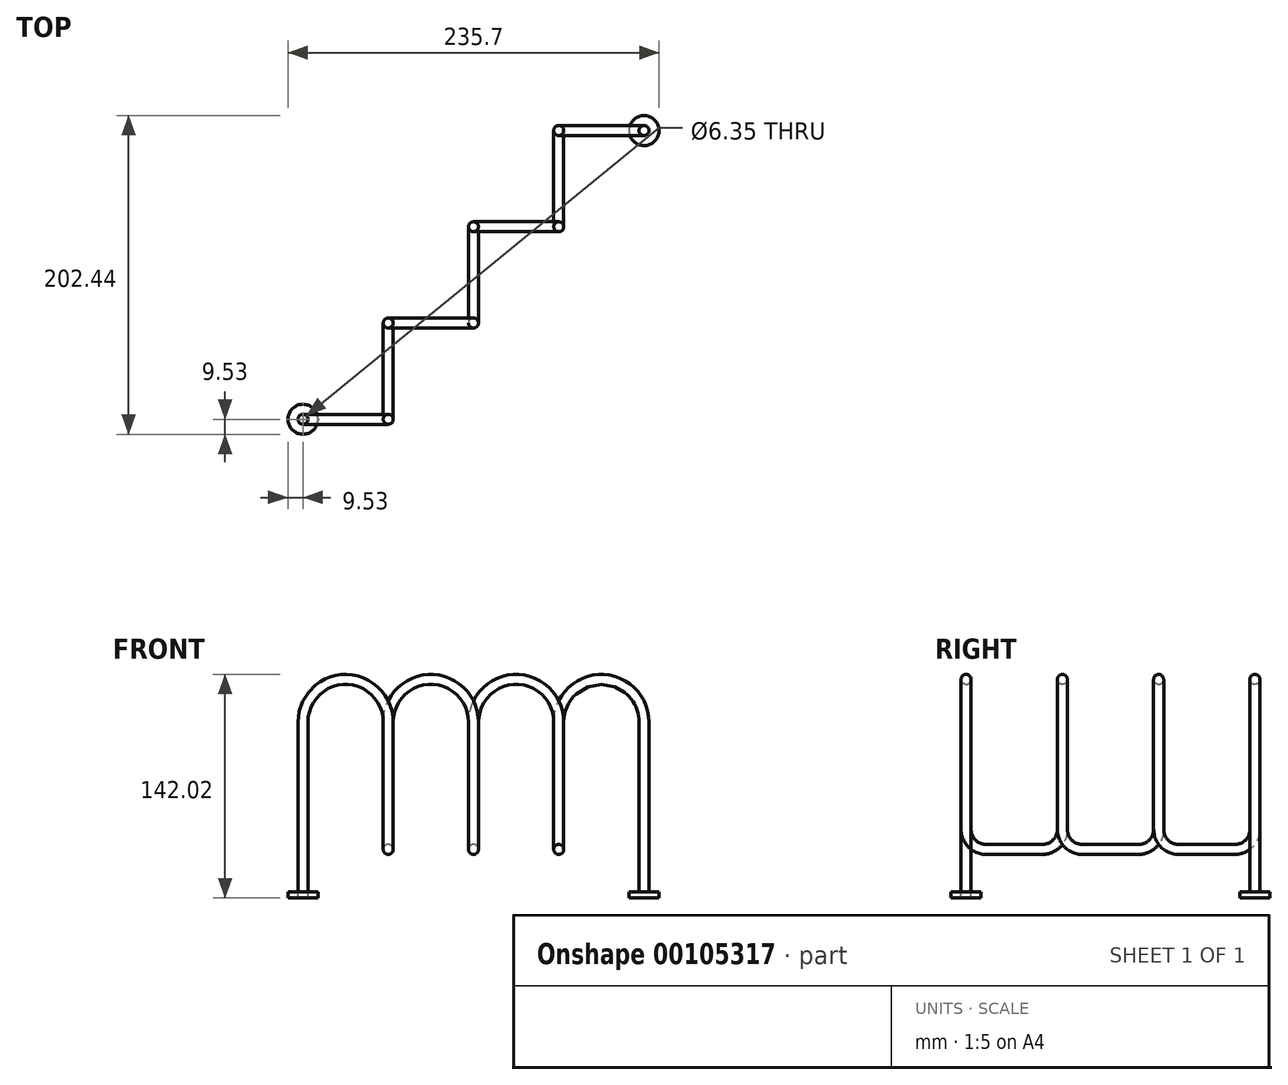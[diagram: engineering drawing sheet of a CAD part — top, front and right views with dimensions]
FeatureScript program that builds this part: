
annotation { "Feature Type Name" : "Feature", "Feature Type Description" : "" }
export const myFeature = defineFeature(function(context is Context, id is Id, definition is map)
    precondition{}
    {
        {
            var Q0;
            Q0=qCreatedBy(makeId("Front.planeOp"),FACE);
            var sketch = newSketch(context, id + "F0", { "sketchPlane" : qUnion([Q0])});
            skLineSegment(sketch, "E0", {"start": v(0, 0) * mm, "end": v(0, -19.05) * mm});
            skLineSegment(sketch, "E1", {"start": v(0, 0) * mm, "end": v(0, 88.9) * mm});
            skArc(sketch, "E2", {"start": v(54.17, 88.9) * mm, "mid": v(27.08, 115.98) * mm, "end": v(0, 88.9) * mm});
            skSolve(sketch);
        }
        {
            var Q0;
            Q0=sQuery(id+"F0.wireOp",VERTEX,"E2.start");
            var Q1;
            Q1=qCreatedBy(makeId("Right.planeOp"),FACE);
            cPlane(context, id + "F1", {"entities" : qUnion([Q0, Q1]), "cplaneType" : CPlaneType.PLANE_POINT, "offset" : 25.4 * mm, "width" : 152.4 * mm, "height" : 152.4 * mm});
        }
        {
            var Q0;
            Q0=qCreatedBy(id+"F1.planeOp",FACE);
            var sketch = newSketch(context, id + "F2", { "sketchPlane" : qUnion([Q0])});
            skLineSegment(sketch, "E3", {"start": v(0, 88.9) * mm, "end": v(0, 20.68) * mm});
            skArc(sketch, "E4", {"start": v(0, 20.68) * mm, "mid": v(3.72, 11.7) * mm, "end": v(12.7, 7.98) * mm});
            skLineSegment(sketch, "E5", {"start": v(12.7, 7.98) * mm, "end": v(48.44, 7.98) * mm});
            skArc(sketch, "E6", {"start": v(48.44, 7.98) * mm, "mid": v(57.42, 11.7) * mm, "end": v(61.14, 20.68) * mm});
            skSolve(sketch);
        }
        {
            var Q0;
            Q0=sQuery(id+"F2.wireOp",VERTEX,"E6.end");
            var Q1;
            Q1=qCreatedBy(makeId("Front.planeOp"),FACE);
            cPlane(context, id + "F3", {"entities" : qUnion([Q0, Q1]), "cplaneType" : CPlaneType.PLANE_POINT, "offset" : 25.4 * mm, "width" : 152.4 * mm, "height" : 152.4 * mm});
        }
        {
            var Q0;
            Q0=qCreatedBy(id+"F3.planeOp",FACE);
            var sketch = newSketch(context, id + "F4", { "sketchPlane" : qUnion([Q0])});
            skLineSegment(sketch, "E7", {"start": v(54.17, 20.68) * mm, "end": v(54.17, 88.9) * mm});
            skArc(sketch, "E8", {"start": v(108.32, 88.9) * mm, "mid": v(81.24, 115.98) * mm, "end": v(54.17, 88.9) * mm});
            skSolve(sketch);
        }
        {
            var Q0;
            Q0=sQuery(id+"F4.wireOp",VERTEX,"E8.start");
            var Q1;
            Q1=qCreatedBy(id+"F1.planeOp",FACE);
            cPlane(context, id + "F5", {"entities" : qUnion([Q0, Q1]), "cplaneType" : CPlaneType.PLANE_POINT, "offset" : 25.4 * mm, "width" : 152.4 * mm, "height" : 152.4 * mm});
        }
        {
            var Q0;
            Q0=qCreatedBy(id+"F5.planeOp",FACE);
            var sketch = newSketch(context, id + "F6", { "sketchPlane" : qUnion([Q0])});
            skLineSegment(sketch, "E9", {"start": v(61.14, 88.9) * mm, "end": v(61.14, 20.68) * mm});
            skArc(sketch, "E10", {"start": v(61.14, 20.68) * mm, "mid": v(64.86, 11.7) * mm, "end": v(73.84, 7.98) * mm});
            skLineSegment(sketch, "E11", {"start": v(73.84, 7.98) * mm, "end": v(109.58, 7.98) * mm});
            skArc(sketch, "E12", {"start": v(109.58, 7.98) * mm, "mid": v(118.56, 11.7) * mm, "end": v(122.28, 20.68) * mm});
            skSolve(sketch);
        }
        {
            var Q0;
            Q0=sQuery(id+"F6.wireOp",VERTEX,"E12.end");
            var Q1;
            Q1=qCreatedBy(makeId("Front.planeOp"),FACE);
            cPlane(context, id + "F7", {"entities" : qUnion([Q0, Q1]), "cplaneType" : CPlaneType.PLANE_POINT, "offset" : 25.4 * mm, "width" : 152.4 * mm, "height" : 152.4 * mm});
        }
        {
            var Q0;
            Q0=qCreatedBy(id+"F7.planeOp",FACE);
            var sketch = newSketch(context, id + "F8", { "sketchPlane" : qUnion([Q0])});
            skLineSegment(sketch, "E13", {"start": v(108.32, 20.68) * mm, "end": v(108.32, 88.9) * mm});
            skArc(sketch, "E14", {"start": v(162.47, 88.9) * mm, "mid": v(135.4, 115.98) * mm, "end": v(108.32, 88.9) * mm});
            skSolve(sketch);
        }
        {
            var Q0;
            Q0=sQuery(id+"F8.wireOp",VERTEX,"E14.start");
            var Q1;
            Q1=qCreatedBy(id+"F1.planeOp",FACE);
            cPlane(context, id + "F9", {"entities" : qUnion([Q0, Q1]), "cplaneType" : CPlaneType.PLANE_POINT, "offset" : 25.4 * mm, "width" : 152.4 * mm, "height" : 152.4 * mm});
        }
        {
            var Q0;
            Q0=qCreatedBy(id+"F9.planeOp",FACE);
            var sketch = newSketch(context, id + "F10", { "sketchPlane" : qUnion([Q0])});
            skLineSegment(sketch, "E15", {"start": v(122.28, 88.9) * mm, "end": v(122.28, 20.68) * mm});
            skArc(sketch, "E16", {"start": v(122.28, 20.68) * mm, "mid": v(126, 11.7) * mm, "end": v(134.98, 7.98) * mm});
            skLineSegment(sketch, "E17", {"start": v(134.98, 7.98) * mm, "end": v(170.72, 7.98) * mm});
            skArc(sketch, "E18", {"start": v(170.72, 7.98) * mm, "mid": v(179.7, 11.7) * mm, "end": v(183.42, 20.68) * mm});
            skSolve(sketch);
        }
        {
            var Q0;
            Q0=sQuery(id+"F10.wireOp",VERTEX,"E18.end");
            var Q1;
            Q1=qCreatedBy(makeId("Front.planeOp"),FACE);
            cPlane(context, id + "F11", {"entities" : qUnion([Q0, Q1]), "cplaneType" : CPlaneType.PLANE_POINT, "offset" : 25.4 * mm, "width" : 152.4 * mm, "height" : 152.4 * mm});
        }
        {
            var Q0;
            Q0=qCreatedBy(id+"F11.planeOp",FACE);
            var sketch = newSketch(context, id + "F12", { "sketchPlane" : qUnion([Q0])});
            skLineSegment(sketch, "E19", {"start": v(162.47, 20.68) * mm, "end": v(162.47, 88.9) * mm});
            skArc(sketch, "E20", {"start": v(216.63, 88.9) * mm, "mid": v(189.55, 115.98) * mm, "end": v(162.47, 88.9) * mm});
            skLineSegment(sketch, "E21", {"start": v(216.63, 88.9) * mm, "end": v(216.63, 0) * mm});
            skLineSegment(sketch, "E22", {"start": v(216.63, 0) * mm, "end": v(216.63, -19.05) * mm});
            skSolve(sketch);
        }
        {
            var Q0;
            Q0=sQuery(id+"F0.wireOp",VERTEX,"E0.end");
            var Q1;
            Q1=qCreatedBy(makeId("Top.planeOp"),FACE);
            cPlane(context, id + "F13", {"entities" : qUnion([Q0, Q1]), "cplaneType" : CPlaneType.PLANE_POINT, "offset" : 25.4 * mm, "width" : 152.4 * mm, "height" : 152.4 * mm});
        }
        {
            var Q0;
            Q0=qCreatedBy(id+"F13.planeOp",FACE);
            var sketch = newSketch(context, id + "F14", { "sketchPlane" : qUnion([Q0])});
            skCircle(sketch, "E23", {"center": v(0, 0) * mm, "radius": 3.18 * mm});
            skCircle(sketch, "E24", {"center": v(0, 0) * mm, "radius": 9.53 * mm});
            skSolve(sketch);
        }
        {
            var Q0;
            Q0=makeQuery(id+"F14.imprint","IMPRINT",FACE,{"disambiguationData":[TD([[makeQuery(id+"F14.imprint","IMPRINT",EDGE,{"derivedFrom":sQuery(id+"F14.wireOp",EDGE,"E23")}),1.0]])]});
            var Q1;
            Q1=sQuery(id+"F0.wireOp",EDGE,"E0");
            var Q2;
            Q2=sQuery(id+"F0.wireOp",EDGE,"E1");
            var Q3;
            Q3=sQuery(id+"F0.wireOp",EDGE,"E2");
            var Q4;
            Q4=sQuery(id+"F2.wireOp",EDGE,"E3");
            var Q5;
            Q5=sQuery(id+"F2.wireOp",EDGE,"E4");
            var Q6;
            Q6=sQuery(id+"F2.wireOp",EDGE,"E5");
            var Q7;
            Q7=sQuery(id+"F2.wireOp",EDGE,"E6");
            var Q8;
            Q8=sQuery(id+"F4.wireOp",EDGE,"E7");
            var Q9;
            Q9=sQuery(id+"F4.wireOp",EDGE,"E8");
            var Q10;
            Q10=sQuery(id+"F6.wireOp",EDGE,"E9");
            var Q11;
            Q11=sQuery(id+"F6.wireOp",EDGE,"E10");
            var Q12;
            Q12=sQuery(id+"F6.wireOp",EDGE,"E11");
            var Q13;
            Q13=sQuery(id+"F6.wireOp",EDGE,"E12");
            var Q14;
            Q14=sQuery(id+"F8.wireOp",EDGE,"E13");
            var Q15;
            Q15=sQuery(id+"F8.wireOp",EDGE,"E14");
            var Q16;
            Q16=sQuery(id+"F10.wireOp",EDGE,"E15");
            var Q17;
            Q17=sQuery(id+"F10.wireOp",EDGE,"E16");
            var Q18;
            Q18=sQuery(id+"F10.wireOp",EDGE,"E17");
            var Q19;
            Q19=sQuery(id+"F10.wireOp",EDGE,"E18");
            var Q20;
            Q20=sQuery(id+"F12.wireOp",EDGE,"E19");
            var Q21;
            Q21=sQuery(id+"F12.wireOp",EDGE,"E20");
            var Q22;
            Q22=sQuery(id+"F12.wireOp",EDGE,"E21");
            var Q23;
            Q23=sQuery(id+"F12.wireOp",EDGE,"E22");
            sweep(context, id + "F15", {"profiles" : qUnion([Q0]), "path" : qUnion([Q1, Q2, Q3, Q4, Q5, Q6, Q7, Q8, Q9, Q10, Q11, Q12, Q13, Q14, Q15, Q16, Q17, Q18, Q19, Q20, Q21, Q22, Q23])});
        }
        {
            var Q0;
            Q0 = qSketchRegion(id + "F14", true);
            extrude(context, id + "F16", {"entities" : qUnion([Q0]), "oppositeDirection" : true, "depth" : 3.8 * mm});
        }
        {
            var Q0;
            Q0=sQuery(id+"F12.wireOp",VERTEX,"E22.end");
            var Q1;
            Q1=qCreatedBy(id+"F13.planeOp",FACE);
            cPlane(context, id + "F17", {"entities" : qUnion([Q0, Q1]), "cplaneType" : CPlaneType.PLANE_POINT, "offset" : 25.4 * mm, "width" : 152.4 * mm, "height" : 152.4 * mm});
        }
        {
            var Q0;
            Q0=qCreatedBy(id+"F17.planeOp",FACE);
            var sketch = newSketch(context, id + "F18", { "sketchPlane" : qUnion([Q0])});
            skCircle(sketch, "E25", {"center": v(216.65, 183.38) * mm, "radius": 9.53 * mm});
            skSolve(sketch);
        }
        {
            var Q0;
            Q0 = qSketchRegion(id + "F18", true);
            extrude(context, id + "F19", {"entities" : qUnion([Q0]), "operationType" : NewBodyOperationType.ADD, "oppositeDirection" : true, "depth" : 3.8 * mm});
        }
    });
